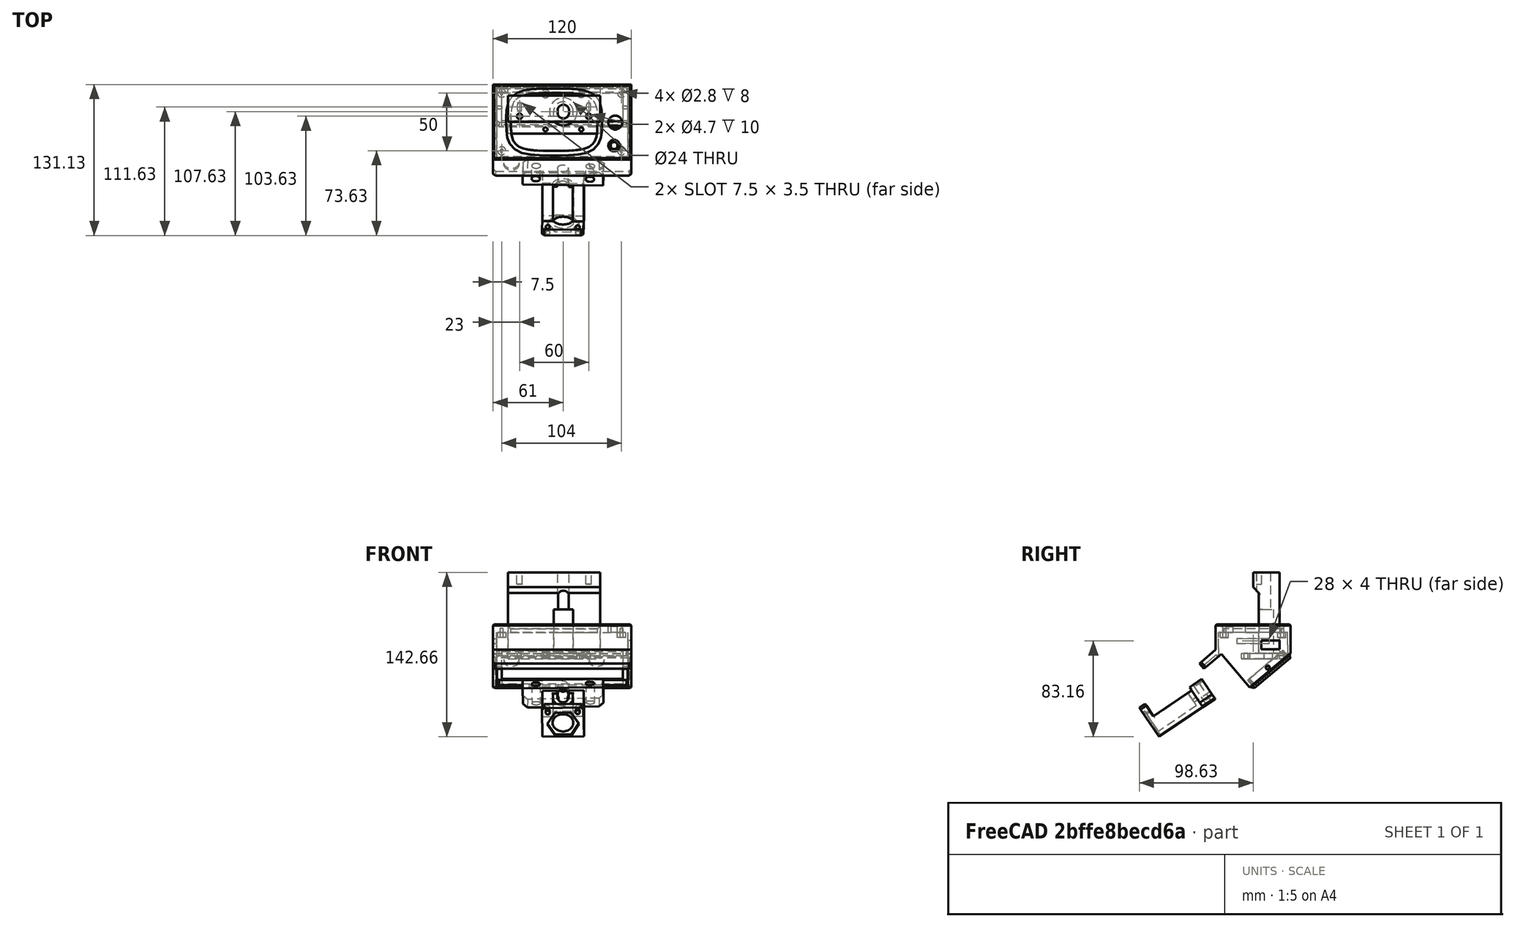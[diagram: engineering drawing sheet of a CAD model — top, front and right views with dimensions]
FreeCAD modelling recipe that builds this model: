
FCSTD DOCUMENT  (FreeCAD 0.19R)
Label: ScreenPodOnly
License: All rights reserved
LicenseURL: http://en.wikipedia.org/wiki/All_rights_reserved
objects: Sketcher::SketchObject×35, PartDesign::Pocket×24, PartDesign::Chamfer×12, PartDesign::Pad×10, PartDesign::Body×5, PartDesign::Fillet×2, Mesh::Feature×2, PartDesign::Mirrored×1
note: 137 computed .brp shape members not serialized (recipe doc carries the construction recipe); baked Part::Feature solids carry a one-line shape summary decoded from their .brp

FEATURE [Sketcher::SketchObject] Sketch
  FullyConstrained = true
  MapMode = 5
  Support = -> [XY_Plane]
  sketch-geometry (30):
    g0: LineSegment StartX=-53 StartY=32.5 StartZ=0 EndX=67 EndY=32.5 EndZ=0
    g1: LineSegment StartX=67 StartY=32.5 StartZ=0 EndX=67 EndY=-32.5 EndZ=0
    g2: LineSegment StartX=67 StartY=-32.5 StartZ=0 EndX=-53 EndY=-32.5 EndZ=0
    g3: LineSegment StartX=-53 StartY=-32.5 StartZ=0 EndX=-53 EndY=32.5 EndZ=0
    g4: LineSegment StartX=-37 StartY=24.5 StartZ=0 EndX=37 EndY=24.5 EndZ=0
    g5: LineSegment StartX=37 StartY=24.5 StartZ=0 EndX=37 EndY=-24.5 EndZ=0
    g6: LineSegment StartX=37 StartY=-24.5 StartZ=0 EndX=-37 EndY=-24.5 EndZ=0
    g7: LineSegment StartX=-37 StartY=-24.5 StartZ=0 EndX=-37 EndY=24.5 EndZ=0
    g8: LineSegment StartX=-37.7408 StartY=25.116 StartZ=0 EndX=37.7408 EndY=25.116 EndZ=0
    g9: LineSegment StartX=37.7408 StartY=25.116 StartZ=0 EndX=37.7408 EndY=-25.116 EndZ=0
    g10: LineSegment StartX=37.7408 StartY=-25.116 StartZ=0 EndX=-37.7408 EndY=-25.116 EndZ=0
    g11: LineSegment StartX=-37.7408 StartY=-25.116 StartZ=0 EndX=-37.7408 EndY=25.116 EndZ=0
    g12-g19: Circle x8 (B-spline internal-alignment scaffolding for g20; pole/knot coordinates omitted)
    g20: BSplineCurve PolesCount=8 KnotsCount=9 Degree=3 IsPeriodic=1
    g21-g29: GeomPoint x9 (B-spline internal-alignment scaffolding for g20; pole/knot coordinates omitted)
  constraints (53):
    c: Coincident(g0,g1)
    c: Coincident(g1,g2)
    c: Coincident(g2,g3)
    c: Coincident(g3,g0)
    c: Horizontal(g0)
    c: Horizontal(g2)
    c: Vertical(g1)
    c: Vertical(g3)
    c: Coincident(g4,g5)
    c: Coincident(g5,g6)
    c: Coincident(g6,g7)
    c: Coincident(g7,g4)
    c: Horizontal(g4)
    c: Vertical(g7)
    c: Distance(g5) = 49
    c: Distance(g4,g3) = 16
    c: Distance(g0,g5) = 30
    c: Distance(g6,g2) = 8
    c: Distance(g4,g0) = 8
    c: Distance(g6) = 74
    c: Symmetric(g5,g6,g-2)
    c: Symmetric(g5,g4,g-1)
    c: Coincident(g8,g9)
    c: Coincident(g9,g10)
    c: Coincident(g10,g11)
    c: Coincident(g11,g8)
    c: Horizontal(g8)
    c: Horizontal(g10)
    c: Vertical(g9)
    c: Vertical(g11)
    c: Symmetric(g9,g8,g-1)
    c: Weight(g12) = 1
    c: Equal(g12,g13)
    c: Equal(g12,g14)
    c: Equal(g12,g15)
    c: PointOnObject(g15,g-1)
    c: Equal(g12,g16)
    c: Equal(g12,g17)
    c: PointOnObject(g17,g-2)
    c: Equal(g12,g18)
    c: Equal(g12,g19)
    c: InternalAlignment(g12-g19 -> g20) x8
    c: InternalAlignment(g21-g29 -> g20) x9
    c: Coincident(g8,g12)
    c: Coincident(g14,g8)
    c: Coincident(g16,g10)
    c: Coincident(g18,g9)
    c: Distance(g19,g5) = 0.5
    c: Symmetric(g19,g15,g-2)
    c: Distance(g17,g6) = 0.5
    c: Symmetric(g17,g13,g-1)
    c: DistanceX(g8) = 37.7408
    c: DistanceY(g8) = 25.116
FEATURE [PartDesign::Pad] Pad
  Direction = (1,1,1)
  Length = 25
  Length2 = 100
  Profile = -> Sketch
  Type = 0
FEATURE [Sketcher::SketchObject] Sketch004  label="knob"
  FullyConstrained = false
  MapMode = 5
  Placement = pos=(0,0,0) rot=(1,0,0;3.14159rad)
  sketch-geometry (1):
    g0: Circle CenterX=52 CenterY=20.5 CenterZ=0 NormalX=0 NormalY=0 NormalZ=1 AngleXU=0 Radius=3
  constraints (1):
    c: Diameter(g0) = 6
FEATURE [PartDesign::Pocket] Pocket001
  BaseFeature = -> Pad
  Length = 5
  Length2 = 100
  Profile = -> Sketch004
  Type = 1
FEATURE [Sketcher::SketchObject] Sketch001  label="knob001"
  FullyConstrained = false
  MapMode = 5
  Placement = pos=(0,0,25) rot=(0,0,1;0rad)
  Support = -> [Pocket001]
  sketch-geometry (1):
    g0: Circle CenterX=53 CenterY=-0.5 CenterZ=0 NormalX=0 NormalY=0 NormalZ=1 AngleXU=0 Radius=6
  constraints (2):
    c: Diameter(g0) = 12
    c: DistanceY(g0) = -0.5
FEATURE [PartDesign::Pocket] Pocket
  BaseFeature = -> Pocket001
  Length = 5
  Length2 = 100
  Profile = -> Sketch001
  Type = 1
FEATURE [Sketcher::SketchObject] Sketch005
  FullyConstrained = true
  MapMode = 5
  Placement = pos=(0,0,0) rot=(1,0,0;3.14159rad)
  Support = -> [Pocket]
  sketch-geometry (4):
    g0: LineSegment StartX=-50 StartY=30 StartZ=0 EndX=64 EndY=30 EndZ=0
    g1: LineSegment StartX=64 StartY=30 StartZ=0 EndX=64 EndY=-30 EndZ=0
    g2: LineSegment StartX=64 StartY=-30 StartZ=0 EndX=-50 EndY=-30 EndZ=0
    g3: LineSegment StartX=-50 StartY=-30 StartZ=0 EndX=-50 EndY=30 EndZ=0
  constraints (11):
    c: Coincident(g0,g1)
    c: Coincident(g1,g2)
    c: Coincident(g2,g3)
    c: Coincident(g3,g0)
    c: Horizontal(g0)
    c: Horizontal(g2)
    c: Vertical(g1)
    c: Symmetric(g2,g0,g-1)
    c: DistanceX(g0) = -50
    c: DistanceY(g0) = 30
    c: DistanceX(g1) = 64
FEATURE [PartDesign::Pocket] Pocket002
  BaseFeature = -> Pocket
  Length = 18
  Length2 = 100
  Profile = -> Sketch005
  Type = 0
FEATURE [PartDesign::Chamfer] Chamfer
  Angle = 45
  Base = -> Pocket002 [Edge19]
  BaseFeature = -> Pocket002
  ChamferType = 0
  FlipDirection = false
  Size = 4
  Size2 = 1
  SupportTransform = false
FEATURE [Sketcher::SketchObject] Sketch006  label="standofs"
  FullyConstrained = true
  MapMode = 5
  Placement = pos=(0,0,18) rot=(1,0,0;3.14159rad)
  Support = -> [Chamfer]
  sketch-geometry (4):
    g0: Circle CenterX=-45.5 CenterY=25 CenterZ=0 NormalX=0 NormalY=0 NormalZ=1 AngleXU=0 Radius=3.5
    g1: Circle CenterX=-45.5 CenterY=-25 CenterZ=0 NormalX=0 NormalY=0 NormalZ=1 AngleXU=0 Radius=3.5
    g2: Circle CenterX=58.5 CenterY=-25 CenterZ=0 NormalX=0 NormalY=0 NormalZ=1 AngleXU=0 Radius=3.5
    g3: Circle CenterX=58.5 CenterY=25 CenterZ=0 NormalX=0 NormalY=0 NormalZ=1 AngleXU=0 Radius=3.5
  constraints (10):
    c: Diameter(g0) = 7
    c: Equal(g0,g1)
    c: Equal(g0,g3)
    c: Equal(g0,g2)
    c: Symmetric(g1,g0,g-1)
    c: Symmetric(g2,g3,g-1)
    c: Distance(g3,g2) = 50
    c: Distance(g1,g0) = 50
    c: Distance(g3,g0) = 104
    c: DistanceX(g0) = -45.5
FEATURE [PartDesign::Pad] Pad001
  BaseFeature = -> Chamfer
  Direction = (1,1,1)
  Length = 4.5
  Length2 = 100
  Profile = -> Sketch006
  Type = 0
FEATURE [Sketcher::SketchObject] Sketch007  label="holes"
  FullyConstrained = true
  MapMode = 5
  Placement = pos=(0,0,13.5) rot=(1,0,0;3.14159rad)
  Support = -> [Pad001]
  sketch-geometry (4):
    g0: Circle CenterX=-45.5 CenterY=25 CenterZ=0 NormalX=0 NormalY=0 NormalZ=1 AngleXU=0 Radius=1.4
    g1: Circle CenterX=58.5 CenterY=25 CenterZ=0 NormalX=0 NormalY=0 NormalZ=1 AngleXU=0 Radius=1.4
    g2: Circle CenterX=58.5 CenterY=-25 CenterZ=0 NormalX=0 NormalY=0 NormalZ=1 AngleXU=0 Radius=1.4
    g3: Circle CenterX=-45.5 CenterY=-25 CenterZ=0 NormalX=0 NormalY=0 NormalZ=1 AngleXU=0 Radius=1.4
  constraints (10):
    c: Distance(g3,g2) = 104
    c: Distance(g3,g0) = 50
    c: Symmetric(g3,g0,g-1)
    c: Symmetric(g2,g1,g-1)
    c: Diameter(g1) = 2.8
    c: Equal(g1,g2)
    c: Equal(g1,g3)
    c: Equal(g1,g0)
    c: DistanceX(g0) = -45.5
    c: Distance(g1,g2) = 50
FEATURE [PartDesign::Pocket] Pocket003
  BaseFeature = -> Pad001
  Length = 8
  Length2 = 100
  Profile = -> Sketch007
  Type = 0
FEATURE [Sketcher::SketchObject] Sketch008
  ExternalGeometry = -> [Pocket003]
  FullyConstrained = true
  MapMode = 5
  Placement = pos=(67,0,0) rot=(0.57735,0.57735,0.57735;2.0944rad)
  Support = -> [Pocket003]
  sketch-geometry (4):
    g0: LineSegment StartX=7 StartY=6.5 StartZ=0 EndX=23 EndY=6.5 EndZ=0
    g1: LineSegment StartX=23 StartY=6.5 StartZ=0 EndX=23 EndY=0 EndZ=0
    g2: LineSegment StartX=23 StartY=0 StartZ=0 EndX=7 EndY=0 EndZ=0
    g3: LineSegment StartX=7 StartY=0 StartZ=0 EndX=7 EndY=6.5 EndZ=0
  constraints (12):
    c: Coincident(g0,g1)
    c: Coincident(g1,g2)
    c: Coincident(g2,g3)
    c: Coincident(g3,g0)
    c: Horizontal(g0)
    c: Horizontal(g2)
    c: Vertical(g1)
    c: Vertical(g3)
    c: Distance(g-3,g0) = 7
    c: Distance(g0) = 16
    c: Distance(g0,g-4) = 7
    c: PointOnObject(g1,g-1)
FEATURE [PartDesign::Pocket] Pocket004
  BaseFeature = -> Pocket003
  Length = 9
  Length2 = 100
  Profile = -> Sketch008
  Type = 0
FEATURE [Sketcher::SketchObject] Sketch009
  ExternalGeometry = -> [Pocket004]
  FullyConstrained = true
  MapMode = 5
  Placement = pos=(-53,0,0) rot=(0.57735,-0.57735,-0.57735;2.0944rad)
  Support = -> [Pocket004]
  sketch-geometry (4):
    g0: LineSegment StartX=-14 StartY=12.5 StartZ=0 EndX=14 EndY=12.5 EndZ=0
    g1: LineSegment StartX=14 StartY=12.5 StartZ=0 EndX=14 EndY=8.5 EndZ=0
    g2: LineSegment StartX=14 StartY=8.5 StartZ=0 EndX=-14 EndY=8.5 EndZ=0
    g3: LineSegment StartX=-14 StartY=8.5 StartZ=0 EndX=-14 EndY=12.5 EndZ=0
  constraints (11):
    c: Coincident(g0,g1)
    c: Coincident(g1,g2)
    c: Coincident(g2,g3)
    c: Coincident(g3,g0)
    c: Horizontal(g0)
    c: Vertical(g1)
    c: Vertical(g3)
    c: Distance(g0,g-3) = 1
    c: Distance(g1) = 4
    c: Symmetric(g1,g2,g-2)
    c: Distance(g2) = 28
FEATURE [PartDesign::Pocket] Pocket005
  BaseFeature = -> Pocket004
  Length = 5
  Length2 = 100
  Profile = -> Sketch009
  Type = 0
FEATURE [Sketcher::SketchObject] Sketch010
  FullyConstrained = false
  MapMode = 5
  Placement = pos=(-53,0,0) rot=(0.57735,-0.57735,-0.57735;2.0944rad)
  Support = -> [Pocket005]
  sketch-geometry (8):
    g0: LineSegment StartX=2.97644 StartY=-29.7683 StartZ=0 EndX=27.4024 EndY=-0.658582 EndZ=0
    g1: LineSegment StartX=27.4024 StartY=-0.658582 StartZ=0 EndX=42.7233 EndY=-13.5143 EndZ=0
    g2: LineSegment StartX=42.7233 StartY=-13.5143 StartZ=0 EndX=46.58 EndY=-8.91807 EndZ=0
    g3: LineSegment StartX=46.58 StartY=-8.91807 StartZ=0 EndX=27.4809 EndY=7.10801 EndZ=0
    g4: LineSegment StartX=-32.5 StartY=0 StartZ=0 EndX=2.97644 EndY=-29.7683 EndZ=0
    g5: LineSegment StartX=2.97644 StartY=-29.7683 StartZ=0 EndX=-60.5281 EndY=23.5183 EndZ=0
    g6: LineSegment StartX=27.4809 StartY=7.10801 StartZ=0 EndX=-32.5 EndY=7.10801 EndZ=0
    g7: LineSegment StartX=-32.5 StartY=7.10801 StartZ=0 EndX=-32.5 EndY=0 EndZ=0
  constraints (21):
    c: Coincident(g0,g1)
    c: Perpendicular(g1,g0)
    c: Coincident(g1,g2)
    c: Coincident(g2,g3)
    c: Coincident(g4,g0)
    c: Distance(g0) = 38
    c: Parallel(g1,g3)
    c: Perpendicular(g0,g4)
    c: Perpendicular(g1,g2)
    c: Distance(g2) = 6
    c: Angle(g0) = 0.872665
    c: Coincident(g5,g0)
    c: Perpendicular(g0,g5)
    c: PointOnObject(g4,g-1)
    c: Distance(g1) = 20
    c: Coincident(g6,g3)
    c: Horizontal(g6)
    c: DistanceX(g6) = -32.5
    c: Coincident(g7,g6)
    c: Vertical(g7)
    c: Coincident(g4,g7)
FEATURE [PartDesign::Pad] Pad002
  BaseFeature = -> Pocket005
  Direction = (1,1,1)
  Length = 120
  Length2 = 100
  Profile = -> Sketch010
  Reversed = true
  Type = 0
FEATURE [Sketcher::SketchObject] Sketch015
  FullyConstrained = true
  MapMode = 5
  Placement = pos=(0,0,13.5) rot=(1,0,0;3.14159rad)
  sketch-geometry (4):
    g0: LineSegment StartX=-50 StartY=30 StartZ=0 EndX=64 EndY=30 EndZ=0
    g1: LineSegment StartX=64 StartY=30 StartZ=0 EndX=64 EndY=-30 EndZ=0
    g2: LineSegment StartX=64 StartY=-30 StartZ=0 EndX=-50 EndY=-30 EndZ=0
    g3: LineSegment StartX=-50 StartY=-30 StartZ=0 EndX=-50 EndY=30 EndZ=0
  constraints (11):
    c: Coincident(g0,g1)
    c: Coincident(g1,g2)
    c: Coincident(g2,g3)
    c: Coincident(g3,g0)
    c: Horizontal(g0)
    c: Horizontal(g2)
    c: Vertical(g1)
    c: DistanceX(g0) = 64
    c: DistanceX(g0) = -50
    c: Distance(g3) = 60
    c: Symmetric(g2,g0,g-1)
FEATURE [PartDesign::Pocket] Pocket006
  BaseFeature = -> Pad002
  Length = 47
  Length2 = 100
  Profile = -> Sketch015
  Reversed = true
  Type = 0
FEATURE [Sketcher::SketchObject] Sketch016
  FullyConstrained = true
  MapMode = 5
  Placement = pos=(67,0,0) rot=(0.57735,0.57735,0.57735;2.0944rad)
  Support = -> [Pocket006]
  sketch-geometry (4):
    g0: LineSegment StartX=7 StartY=11 StartZ=0 EndX=23 EndY=11 EndZ=0
    g1: LineSegment StartX=23 StartY=11 StartZ=0 EndX=23 EndY=3.5 EndZ=0
    g2: LineSegment StartX=23 StartY=3.5 StartZ=0 EndX=7 EndY=3.5 EndZ=0
    g3: LineSegment StartX=7 StartY=3.5 StartZ=0 EndX=7 EndY=11 EndZ=0
  constraints (12):
    c: Coincident(g0,g1)
    c: Coincident(g1,g2)
    c: Coincident(g2,g3)
    c: Coincident(g3,g0)
    c: Horizontal(g0)
    c: Horizontal(g2)
    c: Vertical(g1)
    c: Vertical(g3)
    c: Distance(g1) = 7.5
    c: Distance(g2) = 16
    c: DistanceX(g0) = 7
    c: DistanceY(g0) = 11
FEATURE [PartDesign::Pocket] Pocket007
  BaseFeature = -> Pocket006
  Length = 9
  Length2 = 100
  Profile = -> Sketch016
  Type = 0
FEATURE [PartDesign::Chamfer] Chamfer001
  Angle = 45
  Base = -> Pocket007 [Edge6]
  BaseFeature = -> Pocket007
  ChamferType = 0
  FlipDirection = false
  Size = 2
  Size2 = 1
  SupportTransform = false
FEATURE [Sketcher::SketchObject] Sketch017
  ExternalGeometry = -> [Chamfer001]
  FullyConstrained = false
  MapMode = 5
  Placement = pos=(0,13.4282,-16.0031) rot=(1,0,0;3.83972rad)
  Support = -> [Chamfer001]
  sketch-geometry (4):
    g0: LineSegment StartX=-53 StartY=-24.6078 StartZ=0 EndX=67 EndY=-24.6078 EndZ=0
    g1: LineSegment StartX=67 StartY=-24.6078 StartZ=0 EndX=67 EndY=20.3922 EndZ=0
    g2: LineSegment StartX=67 StartY=20.3922 StartZ=0 EndX=-53 EndY=20.3922 EndZ=0
    g3: LineSegment StartX=-53 StartY=20.3922 StartZ=0 EndX=-53 EndY=-24.6078 EndZ=0
  constraints (11):
    c: Coincident(g0,g1)
    c: Coincident(g1,g2)
    c: Coincident(g2,g3)
    c: Coincident(g3,g0)
    c: Horizontal(g0)
    c: Horizontal(g2)
    c: Vertical(g1)
    c: Vertical(g3)
    c: Distance(g2) = 120
    c: DistanceX(g2) = -53
    c: Distance(g3) = 45
FEATURE [Sketcher::SketchObject] Sketch018
  FullyConstrained = true
  MapMode = 5
  Placement = pos=(0,0,0) rot=(1,0,0;1.5708rad)
  Support = -> [XZ_Plane001]
  sketch-geometry (4):
    g0: LineSegment StartX=-60 StartY=22.5 StartZ=0 EndX=60 EndY=22.5 EndZ=0
    g1: LineSegment StartX=60 StartY=22.5 StartZ=0 EndX=60 EndY=-22.5 EndZ=0
    g2: LineSegment StartX=60 StartY=-22.5 StartZ=0 EndX=-60 EndY=-22.5 EndZ=0
    g3: LineSegment StartX=-60 StartY=-22.5 StartZ=0 EndX=-60 EndY=22.5 EndZ=0
  constraints (10):
    c: Coincident(g0,g1)
    c: Coincident(g1,g2)
    c: Coincident(g2,g3)
    c: Coincident(g3,g0)
    c: Horizontal(g2)
    c: Vertical(g3)
    c: Symmetric(g0,g0,g-2)
    c: Distance(g0) = 120
    c: Distance(g1) = 45
    c: Symmetric(g1,g0,g-1)
FEATURE [PartDesign::Pad] Pad003
  Direction = (1,1,1)
  Length = 3
  Length2 = 100
  Placement = pos=(0,0,0) rot=(1,0,0;1.5708rad)
  Profile = -> Sketch018
  Type = 0
FEATURE [Sketcher::SketchObject] Sketch019
  FullyConstrained = true
  MapMode = 5
  Placement = pos=(0,-3,7e-16) rot=(1,0,0;1.5708rad)
  Support = -> [Pad003]
  sketch-geometry (4):
    g0: LineSegment StartX=-56.75 StartY=20 StartZ=0 EndX=56.75 EndY=20 EndZ=0
    g1: LineSegment StartX=56.75 StartY=20 StartZ=0 EndX=56.75 EndY=-20 EndZ=0
    g2: LineSegment StartX=56.75 StartY=-20 StartZ=0 EndX=-56.75 EndY=-20 EndZ=0
    g3: LineSegment StartX=-56.75 StartY=-20 StartZ=0 EndX=-56.75 EndY=20 EndZ=0
  constraints (11):
    c: Coincident(g0,g1)
    c: Coincident(g1,g2)
    c: Coincident(g2,g3)
    c: Coincident(g3,g0)
    c: Horizontal(g0)
    c: Horizontal(g2)
    c: Vertical(g1)
    c: Vertical(g3)
    c: Distance(g0) = 113.5
    c: Distance(g1) = 40
    c: Symmetric(g1,g0,g-1)
FEATURE [PartDesign::Pad] Pad004
  BaseFeature = -> Pad003
  Direction = (1,1,1)
  Length = 6
  Length2 = 100
  Placement = pos=(0,0,0) rot=(1,0,0;1.5708rad)
  Profile = -> Sketch019
  Type = 0
FEATURE [Sketcher::SketchObject] Sketch020
  FullyConstrained = true
  MapMode = 5
  Placement = pos=(56.75,0,0) rot=(0.707107,0,0.707107;3.14159rad)
  Support = -> [Pad004]
  sketch-geometry (1):
    g0: Circle CenterX=0 CenterY=6 CenterZ=0 NormalX=0 NormalY=0 NormalZ=1 AngleXU=0 Radius=1.4
  constraints (3):
    c: PointOnObject(g0,g-2)
    c: Diameter(g0) = 2.8
    c: DistanceY(g0) = 6
FEATURE [PartDesign::Pocket] Pocket008
  BaseFeature = -> Pad004
  Length = 5
  Length2 = 100
  Placement = pos=(0,0,0) rot=(1,0,0;1.5708rad)
  Profile = -> Sketch020
  Type = 1
FEATURE [Sketcher::SketchObject] Sketch021
  FullyConstrained = true
  MapMode = 5
  Placement = pos=(0,-9,1.5e-14) rot=(1,0,0;1.5708rad)
  sketch-geometry (4):
    g0: LineSegment StartX=-52.5 StartY=18.5 StartZ=0 EndX=52.5 EndY=18.5 EndZ=0
    g1: LineSegment StartX=52.5 StartY=18.5 StartZ=0 EndX=52.5 EndY=-18.5 EndZ=0
    g2: LineSegment StartX=52.5 StartY=-18.5 StartZ=0 EndX=-52.5 EndY=-18.5 EndZ=0
    g3: LineSegment StartX=-52.5 StartY=-18.5 StartZ=0 EndX=-52.5 EndY=18.5 EndZ=0
  constraints (11):
    c: Coincident(g0,g1)
    c: Coincident(g1,g2)
    c: Coincident(g2,g3)
    c: Coincident(g3,g0)
    c: Horizontal(g0)
    c: Horizontal(g2)
    c: Vertical(g1)
    c: Vertical(g3)
    c: Distance(g0) = 105
    c: Symmetric(g0,g2,g-1)
    c: Distance(g1) = 37
FEATURE [Sketcher::SketchObject] Sketch022
  ExternalGeometry = -> [Chamfer001]
  FullyConstrained = true
  MapMode = 5
  Placement = pos=(-53,0,0) rot=(0.57735,-0.57735,-0.57735;2.0944rad)
  Support = -> [Chamfer001]
  sketch-geometry (2):
    g0: Circle CenterX=-12.8334 CenterY=-12.586 CenterZ=0 NormalX=0 NormalY=0 NormalZ=1 AngleXU=0 Radius=1.75
    g1: LineSegment StartX=-30.5716 StartY=2.29813 StartZ=0 EndX=4.90481 EndY=-27.4701 EndZ=0
  constraints (6):
    c: Parallel(g1,g-3)
    c: Distance(g1,g-3) = 3
    c: Equal(g1,g-3)
    c: Symmetric(g1,g1,g0)
    c: Diameter(g0) = 3.5
    c: PointOnObject(g1,g-4)
FEATURE [PartDesign::Pocket] Pocket010
  BaseFeature = -> Chamfer001
  Length = 5
  Length2 = 100
  Profile = -> Sketch022
  Type = 1
FEATURE [PartDesign::Chamfer] Chamfer005
  Angle = 45
  Base = -> Pocket010 [Edge97]
  BaseFeature = -> Pocket010
  ChamferType = 0
  FlipDirection = false
  Size = 2
  Size2 = 1
  SupportTransform = false
FEATURE [PartDesign::Chamfer] Chamfer006
  Angle = 45
  Base = -> Chamfer005 [Edge23]
  BaseFeature = -> Chamfer005
  ChamferType = 0
  FlipDirection = false
  Size = 2
  Size2 = 1
  SupportTransform = false
FEATURE [Sketcher::SketchObject] Sketch023
  FullyConstrained = true
  MapMode = 5
  Placement = pos=(0,-10.9977,13.1066) rot=(1,0,0;3.83972rad)
  Support = -> [Chamfer006]
  sketch-geometry (2):
    g0: Circle CenterX=-37 CenterY=32 CenterZ=0 NormalX=0 NormalY=0 NormalZ=1 AngleXU=0 Radius=6.5
    g1: Circle CenterX=37 CenterY=32 CenterZ=0 NormalX=0 NormalY=0 NormalZ=1 AngleXU=0 Radius=6.5
  constraints (5):
    c: Diameter(g1) = 13
    c: Equal(g1,g0)
    c: Symmetric(g1,g0,g-2)
    c: DistanceY(g0) = 32
    c: Distance(g1,g0) = 74
FEATURE [PartDesign::Pocket] Pocket011
  BaseFeature = -> Chamfer006
  Length = 2.3
  Length2 = 100
  Profile = -> Sketch023
  Type = 0
FEATURE [PartDesign::Chamfer] Chamfer007
  Angle = 45
  Base = -> Pocket011 [Edge74,Edge75,Edge31,Edge67]
  BaseFeature = -> Pocket011
  ChamferType = 0
  FlipDirection = false
  Size = 1
  Size2 = 1
  SupportTransform = false
FEATURE [PartDesign::Body] Body  label="ScreenBox"
  Group = -> [Sketch,Pad,Sketch001,Sketch004,Pocket001,Pocket,Sketch005,Pocket002,Chamfer,Sketch006,Pad001,Sketch007,Pocket003,Sketch008,Pocket004,Sketch009,Pocket005,Sketch010,Pad002,Sketch015,Pocket006,Sketch016,Pocket007,Chamfer001,Sketch017,Sketch022,Pocket010,Chamfer005,Chamfer006,Sketch023,Pocket011,Chamfer007]
  Origin = -> Origin
  Tip = -> Chamfer007
FEATURE [Sketcher::SketchObject] Sketch024
  ExternalGeometry = -> [Pocket008]
  FullyConstrained = false
  MapMode = 5
  Placement = pos=(60,0,0) rot=(0.707107,0,0.707107;3.14159rad)
  Support = -> [Pocket008]
  sketch-geometry (3):
    g0: LineSegment StartX=-22.5 StartY=3 StartZ=0 EndX=-17.8755 EndY=-3.60453 EndZ=0
    g1: LineSegment StartX=-17.8755 StartY=-3.60453 StartZ=0 EndX=-35.5163 EndY=-3.60453 EndZ=0
    g2: LineSegment StartX=-35.5163 StartY=-3.60453 StartZ=0 EndX=-22.5 EndY=3 EndZ=0
  constraints (6):
    c: Coincident(g0,g1)
    c: Horizontal(g1)
    c: Coincident(g1,g2)
    c: Coincident(g2,g0)
    c: Angle(g0) = -0.959931
    c: Coincident(g0,g-3)
FEATURE [PartDesign::Pocket] Pocket012
  BaseFeature = -> Pocket008
  Length = 5
  Length2 = 100
  Placement = pos=(0,0,0) rot=(1,0,0;1.5708rad)
  Profile = -> Sketch024
  Type = 1
FEATURE [PartDesign::Mirrored] Mirrored
  BaseFeature = -> Pocket012
  MirrorPlane = -> Sketch024 [V_Axis]
  Originals = -> [Pocket012]
  Placement = pos=(0,0,0) rot=(1,0,0;1.5708rad)
FEATURE [PartDesign::Chamfer] Chamfer008
  Angle = 45
  Base = -> Mirrored [Edge14,Edge12]
  BaseFeature = -> Mirrored
  ChamferType = 0
  FlipDirection = false
  Placement = pos=(0,0,0) rot=(1,0,0;1.5708rad)
  Size = 2
  Size2 = 1
  SupportTransform = false
FEATURE [PartDesign::Pocket] Pocket013
  BaseFeature = -> Chamfer008
  Length = 6
  Length2 = 100
  Placement = pos=(0,0,0) rot=(1,0,0;1.5708rad)
  Profile = -> Sketch021
  Type = 0
FEATURE [PartDesign::Chamfer] Chamfer009
  Angle = 45
  Base = -> Pocket013 [Edge29]
  BaseFeature = -> Pocket013
  ChamferType = 0
  FlipDirection = false
  Placement = pos=(0,0,0) rot=(1,0,0;1.5708rad)
  Size = 2
  Size2 = 1
  SupportTransform = false
FEATURE [PartDesign::Chamfer] Chamfer010
  Angle = 45
  Base = -> Chamfer009 [Edge11]
  BaseFeature = -> Chamfer009
  ChamferType = 0
  FlipDirection = false
  Placement = pos=(0,0,0) rot=(1,0,0;1.5708rad)
  Size = 1
  Size2 = 1
  SupportTransform = false
FEATURE [PartDesign::Chamfer] Chamfer011
  Angle = 45
  Base = -> Chamfer010 [Edge18]
  BaseFeature = -> Chamfer010
  ChamferType = 0
  FlipDirection = false
  Placement = pos=(0,0,0) rot=(1,0,0;1.5708rad)
  Size = 1
  Size2 = 1
  SupportTransform = false
FEATURE [PartDesign::Chamfer] Chamfer012
  Angle = 45
  Base = -> Chamfer011 [Edge20]
  BaseFeature = -> Chamfer011
  ChamferType = 0
  FlipDirection = false
  Placement = pos=(0,0,0) rot=(1,0,0;1.5708rad)
  Size = 2
  Size2 = 1
  SupportTransform = false
FEATURE [PartDesign::Body] Body001  label="BoxCap"
  Group = -> [Sketch018,Pad003,Sketch019,Pad004,Sketch020,Pocket008,Sketch021,Sketch024,Pocket012,Mirrored,Chamfer008,Pocket013,Chamfer009,Chamfer010,Chamfer011,Chamfer012]
  Origin = -> Origin001
  Placement = pos=(7,16.6296,-17.3502) rot=(-1,0,0;0.872665rad)
  Tip = -> Chamfer012
FEATURE [Sketcher::SketchObject] Sketch025  label="mountSlots"
  FullyConstrained = true
  MapMode = 5
  Placement = pos=(0,20.9938,0) rot=(0,0.707107,0.707107;3.14159rad)
  sketch-geometry (9):
    g0: ArcOfCircle CenterX=-16.5 CenterY=6.35 CenterZ=0 NormalX=0 NormalY=0 NormalZ=1 AngleXU=0 Radius=2.6 StartAngle=1.5708 EndAngle=4.71239
    g1: ArcOfCircle CenterX=-14.5 CenterY=6.35 CenterZ=0 NormalX=0 NormalY=0 NormalZ=1 AngleXU=0 Radius=2.6 StartAngle=4.71239 EndAngle=7.85398
    g2: LineSegment StartX=-16.5 StartY=3.75 StartZ=0 EndX=-14.5 EndY=3.75 EndZ=0
    g3: LineSegment StartX=-16.5 StartY=8.95 StartZ=0 EndX=-14.5 EndY=8.95 EndZ=0
    g4: ArcOfCircle CenterX=30.5 CenterY=6.35 CenterZ=0 NormalX=0 NormalY=0 NormalZ=1 AngleXU=0 Radius=2.6 StartAngle=1.5708 EndAngle=4.71239
    g5: ArcOfCircle CenterX=32.5 CenterY=6.35 CenterZ=0 NormalX=0 NormalY=0 NormalZ=1 AngleXU=0 Radius=2.6 StartAngle=4.71239 EndAngle=7.85398
    g6: LineSegment StartX=30.5 StartY=3.75 StartZ=0 EndX=32.5 EndY=3.75 EndZ=0
    g7: LineSegment StartX=30.5 StartY=8.95 StartZ=0 EndX=32.5 EndY=8.95 EndZ=0
    g8: Circle CenterX=8 CenterY=6.35 CenterZ=0 NormalX=0 NormalY=0 NormalZ=1 AngleXU=0 Radius=0.77
  constraints (22):
    c: Tangent(g0,g3) = 1.5708
    c: Tangent(g0,g2) = -1.5708
    c: Tangent(g2,g1) = -1.5708
    c: Tangent(g3,g1) = 1.5708
    c: Horizontal(g2)
    c: Equal(g0,g1)
    c: Tangent(g4,g7) = 1.5708
    c: Tangent(g4,g6) = -1.5708
    c: Tangent(g6,g5) = -1.5708
    c: Tangent(g7,g5) = 1.5708
    c: Horizontal(g6)
    c: Equal(g4,g5)
    c: Distance(g1,g1) = 5.2
    c: Distance(g5,g5) = 5.2
    c: DistanceY(g1) = 6.35
    c: Distance(g6) = 2
    c: Distance(g2) = 2
    c: Distance(g1,g4) = 45
    c: Symmetric(g1,g4,g8)
    c: DistanceX(g8) = 8
    c: DistanceY(g5) = 6.35
    c: Diameter(g8) = 1.54
FEATURE [Sketcher::SketchObject] Sketch026  label="hex"
  FullyConstrained = true
  MapMode = 5
  Placement = pos=(0,0,56.7) rot=(0,0,1;0rad)
  sketch-geometry (8):
    g0: Circle CenterX=-8 CenterY=5 CenterZ=0 NormalX=0 NormalY=0 NormalZ=1 AngleXU=0 Radius=11
    g1: LineSegment StartX=5.85641 StartY=5 StartZ=0 EndX=-1.0718 EndY=17 EndZ=0
    g2: LineSegment StartX=-1.0718 StartY=17 StartZ=0 EndX=-14.9282 EndY=17 EndZ=0
    g3: LineSegment StartX=-14.9282 StartY=17 StartZ=0 EndX=-21.8564 EndY=5 EndZ=0
    g4: LineSegment StartX=-21.8564 StartY=5 StartZ=0 EndX=-14.9282 EndY=-7 EndZ=0
    g5: LineSegment StartX=-14.9282 StartY=-7 StartZ=0 EndX=-1.0718 EndY=-7 EndZ=0
    g6: LineSegment StartX=-1.0718 StartY=-7 StartZ=0 EndX=5.85641 EndY=5 EndZ=0
    g7: Circle CenterX=-8 CenterY=5 CenterZ=0 NormalX=0 NormalY=0 NormalZ=1 AngleXU=0 Radius=13.8564
  constraints (19):
    c: Diameter(g0) = 22
    c: DistanceX(g0) = -8
    c: DistanceY(g0) = 5
    c: Coincident(g1,g2)
    c: Coincident(g2,g3)
    c: Coincident(g3,g4)
    c: Coincident(g4,g5)
    c: Coincident(g5,g6)
    c: Coincident(g6,g1)
    c: Equal(g1, g2-g6) x5
    c: PointOnObject(g1,g7)
    c: PointOnObject(g2,g7)
    c: PointOnObject(g3,g7)
    c: PointOnObject(g4,g7)
    c: PointOnObject(g5,g7)
    c: PointOnObject(g6,g7)
    c: Coincident(g7,g0)
    c: Distance(g1,g4) = 24
    c: Horizontal(g2)
FEATURE [Sketcher::SketchObject] Sketch027  label="StepperPlatform"
  FullyConstrained = false
  MapMode = 5
  Placement = pos=(0,0,52.7) rot=(0,0,1;0rad)
  sketch-geometry (22):
    g0: Circle CenterX=-21 CenterY=18 CenterZ=0 NormalX=0 NormalY=0 NormalZ=1 AngleXU=0 Radius=1.4
    g1: Circle CenterX=5 CenterY=18 CenterZ=0 NormalX=0 NormalY=0 NormalZ=1 AngleXU=0 Radius=1.4
    g2: Circle CenterX=-21 CenterY=-8 CenterZ=0 NormalX=0 NormalY=0 NormalZ=1 AngleXU=0 Radius=1.4
    g3: Circle CenterX=5 CenterY=-8 CenterZ=0 NormalX=0 NormalY=0 NormalZ=1 AngleXU=0 Radius=1.4
    g4: LineSegment StartX=-21 StartY=18 StartZ=0 EndX=5 EndY=18 EndZ=0
    g5: LineSegment StartX=5 StartY=18 StartZ=0 EndX=5 EndY=-8 EndZ=0
    g6: LineSegment StartX=5 StartY=-8 StartZ=0 EndX=-21 EndY=-8 EndZ=0
    g7: LineSegment StartX=-21 StartY=-8 StartZ=0 EndX=-21 EndY=18 EndZ=0
    g8: Circle CenterX=-8 CenterY=5 CenterZ=0 NormalX=0 NormalY=0 NormalZ=1 AngleXU=0 Radius=1.66613
    g9: LineSegment StartX=-26 StartY=18 StartZ=0 EndX=10 EndY=18 EndZ=0
    g10: LineSegment StartX=10 StartY=18 StartZ=0 EndX=10 EndY=-12 EndZ=0
    g11: LineSegment StartX=10 StartY=-12 StartZ=0 EndX=-26 EndY=-12 EndZ=0
    g12: LineSegment StartX=-26 StartY=-12 StartZ=0 EndX=-26 EndY=18 EndZ=0
    g13: LineSegment StartX=-8 StartY=22.1839 StartZ=0 EndX=-8 EndY=5 EndZ=0
    g14: ArcOfCircle CenterX=-21 CenterY=-7 CenterZ=0 NormalX=0 NormalY=0 NormalZ=1 AngleXU=0 Radius=1.75 StartAngle=0 EndAngle=3.14159
    g15: ArcOfCircle CenterX=-21 CenterY=-9 CenterZ=0 NormalX=0 NormalY=0 NormalZ=1 AngleXU=0 Radius=1.75 StartAngle=3.14159 EndAngle=6.28319
    g16: LineSegment StartX=-22.75 StartY=-7 StartZ=0 EndX=-22.75 EndY=-9 EndZ=0
    g17: LineSegment StartX=-19.25 StartY=-7 StartZ=0 EndX=-19.25 EndY=-9 EndZ=0
    g18: ArcOfCircle CenterX=5 CenterY=-7 CenterZ=0 NormalX=0 NormalY=0 NormalZ=1 AngleXU=0 Radius=1.75 StartAngle=1e-16 EndAngle=3.14159
    g19: ArcOfCircle CenterX=5 CenterY=-9 CenterZ=0 NormalX=0 NormalY=0 NormalZ=1 AngleXU=0 Radius=1.75 StartAngle=3.14159 EndAngle=6.28319
    g20: LineSegment StartX=3.25 StartY=-7 StartZ=0 EndX=3.25 EndY=-9 EndZ=0
    g21: LineSegment StartX=6.75 StartY=-7 StartZ=0 EndX=6.75 EndY=-9 EndZ=0
  constraints (52):
    c: Coincident(g4,g0)
    c: Coincident(g4,g1)
    c: Horizontal(g4)
    c: Coincident(g4,g5)
    c: Coincident(g5,g3)
    c: Coincident(g5,g6)
    c: Coincident(g6,g2)
    c: Horizontal(g6)
    c: Coincident(g6,g7)
    c: Coincident(g7,g4)
    c: Distance(g7) = 26
    c: Equal(g7,g4)
    c: Equal(g4,g5)
    c: Vertical(g7)
    c: DistanceX(g8) = -8
    c: DistanceY(g8) = 5
    c: Diameter(g0) = 2.8
    c: Equal(g0,g1)
    c: Equal(g0,g3)
    c: Equal(g0,g2)
    c: Coincident(g9,g10)
    c: Coincident(g10,g11)
    c: Coincident(g11,g12)
    c: Coincident(g12,g9)
    c: Horizontal(g9)
    c: Horizontal(g11)
    c: Vertical(g10)
    c: Vertical(g12)
    c: Distance(g9) = 36
    c: Coincident(g13,g8)
    c: Tangent(g14,g17) = 1.5708
    c: Tangent(g14,g16) = -1.5708
    c: Tangent(g16,g15) = -1.5708
    c: Tangent(g17,g15) = 1.5708
    c: Vertical(g16)
    c: Equal(g14,g15)
    c: PointOnObject(g14,g7)
    c: Distance(g14,g2) = 1
    c: Distance(g15,g2) = 1
    c: Tangent(g18,g21) = 1.5708
    c: Tangent(g18,g20) = -1.5708
    c: Tangent(g20,g19) = -1.5708
    c: Tangent(g21,g19) = 1.5708
    c: Vertical(g20)
    c: Equal(g18,g19)
    c: PointOnObject(g18,g5)
    c: Distance(g18,g3) = 1
    c: Distance(g19,g3) = 1
    c: Diameter(g18) = 3.5
    c: Diameter(g14) = 3.5
    c: DistanceY(g9) = 18
    c: DistanceY(g10) = -12
FEATURE [Sketcher::SketchObject] Sketch028  label="leadSlot"
  FullyConstrained = true
  MapMode = 5
  Placement = pos=(0,0,52.7) rot=(0,0,1;0rad)
  sketch-geometry (4):
    g0: ArcOfCircle CenterX=-8 CenterY=5 CenterZ=0 NormalX=0 NormalY=0 NormalZ=1 AngleXU=0 Radius=5 StartAngle=2e-16 EndAngle=3.14159
    g1: LineSegment StartX=-3 StartY=5 StartZ=0 EndX=-3 EndY=-7.39 EndZ=0
    g2: LineSegment StartX=-3 StartY=-7.39 StartZ=0 EndX=-13 EndY=-7.39 EndZ=0
    g3: LineSegment StartX=-13 StartY=-7.39 StartZ=0 EndX=-13 EndY=5 EndZ=0
  constraints (11):
    c: Tangent(g0,g1) = 1.5708
    c: Coincident(g1,g2)
    c: Horizontal(g2)
    c: Coincident(g2,g3)
    c: Vertical(g3)
    c: Diameter(g0) = 10
    c: Vertical(g1)
    c: DistanceX(g0) = -8
    c: DistanceY(g0) = 5
    c: Tangent(g3,g0) = 1.5708
    c: Distance(g1) = 12.39
FEATURE [Sketcher::SketchObject] Sketch029  label="BottomBit"
  FullyConstrained = false
  MapMode = 5
  Support = -> [XY_Plane002]
  sketch-geometry (5):
    g0: LineSegment StartX=-43 StartY=18 StartZ=0 EndX=27 EndY=18 EndZ=0
    g1: LineSegment StartX=27 StartY=-2 StartZ=0 EndX=-43 EndY=-2 EndZ=0
    g2: LineSegment StartX=27 StartY=18 StartZ=0 EndX=27 EndY=-2 EndZ=0
    g3: LineSegment StartX=-43 StartY=18 StartZ=0 EndX=-43 EndY=-2 EndZ=0
    g4: LineSegment StartX=-8 StartY=20.77 StartZ=0 EndX=-8 EndY=17.2529 EndZ=0
  constraints (13):
    c: Horizontal(g1)
    c: DistanceY(g1) = -2
    c: DistanceY(g0) = 18
    c: Coincident(g2,g0)
    c: Vertical(g2)
    c: Coincident(g3,g0)
    c: Vertical(g3)
    c: Coincident(g3,g1)
    c: Coincident(g1,g2)
    c: Horizontal(g0)
    c: Symmetric(g0,g0,g4)
    c: DistanceX(g4) = -8
    c: Distance(g0) = 70
FEATURE [PartDesign::Pad] Pad005
  Direction = (1,1,1)
  Length = 12.7
  Length2 = 100
  Profile = -> Sketch029
  Type = 0
FEATURE [Sketcher::SketchObject] Sketch012  label="towerProper"
  FullyConstrained = false
  MapMode = 5
  Placement = pos=(0,0,12.7) rot=(0,0,1;0rad)
  Support = -> [Pad005]
  sketch-geometry (5):
    g0: LineSegment StartX=-26 StartY=18 StartZ=0 EndX=10 EndY=18 EndZ=0
    g1: LineSegment StartX=10 StartY=18 StartZ=0 EndX=10 EndY=1 EndZ=0
    g2: LineSegment StartX=10 StartY=1 StartZ=0 EndX=-26 EndY=1 EndZ=0
    g3: LineSegment StartX=-26 StartY=1 StartZ=0 EndX=-26 EndY=18 EndZ=0
    g4: LineSegment StartX=-8 StartY=21.6614 StartZ=0 EndX=-8 EndY=16.5307 EndZ=0
  constraints (13):
    c: Coincident(g0,g1)
    c: Coincident(g1,g2)
    c: Coincident(g2,g3)
    c: Coincident(g3,g0)
    c: Horizontal(g2)
    c: Vertical(g1)
    c: Vertical(g3)
    c: Distance(g0) = 36
    c: Vertical(g4)
    c: Symmetric(g0,g0,g4)
    c: DistanceX(g4) = -8
    c: DistanceY(g0) = 18
    c: DistanceY(g1) = 1
FEATURE [PartDesign::Pad] Pad006
  BaseFeature = -> Pad005
  Direction = (1,1,1)
  Length = 40
  Length2 = 100
  Profile = -> Sketch012
  Type = 0
FEATURE [PartDesign::Pocket] Pocket016
  BaseFeature = -> Pad006
  Length = 40
  Length2 = 100
  Profile = -> Sketch028
  Type = 0
FEATURE [PartDesign::Pocket] Pocket014
  BaseFeature = -> Pocket016
  Length = 5
  Length2 = 100
  Profile = -> Sketch025
  Type = 1
FEATURE [PartDesign::Pad] Pad007
  BaseFeature = -> Pocket014
  Direction = (1,1,1)
  Length = 6
  Length2 = 100
  Profile = -> Sketch027
  Type = 0
FEATURE [PartDesign::Pocket] Pocket017
  BaseFeature = -> Pad007
  Length = 2
  Length2 = 100
  Profile = -> Sketch026
  Reversed = true
  Type = 0
FEATURE [Sketcher::SketchObject] Sketch030  label="leadscrew"
  FullyConstrained = true
  MapMode = 5
  Placement = pos=(0,0,12.7) rot=(0,0,1;0rad)
  sketch-geometry (4):
    g0: ArcOfCircle CenterX=-8 CenterY=6 CenterZ=0 NormalX=0 NormalY=0 NormalZ=1 AngleXU=0 Radius=4.5 StartAngle=1e-16 EndAngle=3.14159
    g1: ArcOfCircle CenterX=-8 CenterY=4 CenterZ=0 NormalX=0 NormalY=0 NormalZ=1 AngleXU=0 Radius=4.5 StartAngle=3.14159 EndAngle=6.28319
    g2: LineSegment StartX=-12.5 StartY=6 StartZ=0 EndX=-12.5 EndY=4 EndZ=0
    g3: LineSegment StartX=-3.5 StartY=6 StartZ=0 EndX=-3.5 EndY=4 EndZ=0
  constraints (10):
    c: Tangent(g0,g3) = 1.5708
    c: Tangent(g0,g2) = -1.5708
    c: Tangent(g2,g1) = -1.5708
    c: Tangent(g3,g1) = 1.5708
    c: Vertical(g2)
    c: Equal(g0,g1)
    c: DistanceY(g1) = 4
    c: DistanceY(g0) = 6
    c: DistanceX(g0) = -8
    c: Diameter(g0) = 9
FEATURE [PartDesign::Pocket] Pocket015
  BaseFeature = -> Pocket017
  Length = 22
  Length2 = 100
  Profile = -> Sketch030
  Type = 4
FEATURE [Sketcher::SketchObject] Sketch013  label="counterbore"
  FullyConstrained = true
  MapMode = 5
  Placement = pos=(0,0,56.7) rot=(0,0,1;0rad)
  Support = -> [Pocket015]
  sketch-geometry (1):
    g0: Circle CenterX=-8 CenterY=5 CenterZ=0 NormalX=0 NormalY=0 NormalZ=1 AngleXU=0 Radius=9
  constraints (3):
    c: DistanceX(g0) = -8
    c: DistanceY(g0) = 5
    c: Diameter(g0) = 18
FEATURE [PartDesign::Pocket] Pocket018
  BaseFeature = -> Pocket015
  Length = 40
  Length2 = 100
  Profile = -> Sketch013
  Type = 0
FEATURE [PartDesign::Fillet] Fillet
  Base = -> Pocket018 [Edge83,Edge72]
  BaseFeature = -> Pocket018
  Radius = 1
  SupportTransform = false
FEATURE [PartDesign::Chamfer] Chamfer014
  Angle = 45
  Base = -> Fillet [Edge52,Edge57]
  BaseFeature = -> Fillet
  ChamferType = 0
  FlipDirection = false
  Size = 2
  Size2 = 1
  SupportTransform = false
FEATURE [PartDesign::Chamfer] Chamfer013
  Angle = 45
  Base = -> Chamfer014 [Edge135,Edge133]
  BaseFeature = -> Chamfer014
  ChamferType = 0
  FlipDirection = false
  Size = 4
  Size2 = 1
  SupportTransform = false
FEATURE [PartDesign::Body] Body002  label="Ztower"
  Group = -> [Sketch029,Pad005,Sketch028,Sketch030,Sketch027,Sketch026,Sketch025,Sketch012,Pad006,Pocket016,Pocket014,Pad007,Pocket017,Pocket015,Sketch013,Pocket018,Fillet,Chamfer014,Chamfer013]
  Origin = -> Origin002
  Placement = pos=(-0.401038,-43.0056,-24.8059) rot=(0.007695,0.882707,-0.469861;3.13341rad)
  Tip = -> Chamfer013
FEATURE [Sketcher::SketchObject] Sketch039
  FullyConstrained = true
  MapMode = 5
  Placement = pos=(0,0,0) rot=(0.57735,0.57735,0.57735;2.0944rad)
  Support = -> [YZ_Plane003]
  sketch-geometry (6):
    g0: LineSegment StartX=0 StartY=70 StartZ=0 EndX=23 EndY=70 EndZ=0
    g1: LineSegment StartX=23 StartY=70 StartZ=0 EndX=23 EndY=0 EndZ=0
    g2: LineSegment StartX=23 StartY=0 StartZ=0 EndX=5 EndY=0 EndZ=0
    g3: LineSegment StartX=5 StartY=0 StartZ=0 EndX=5 EndY=52.3 EndZ=0
    g4: LineSegment StartX=5 StartY=52.3 StartZ=0 EndX=0 EndY=57.3 EndZ=0
    g5: LineSegment StartX=0 StartY=57.3 StartZ=0 EndX=0 EndY=70 EndZ=0
  constraints (18):
    c: PointOnObject(g0,g-2)
    c: Horizontal(g0)
    c: Coincident(g0,g1)
    c: PointOnObject(g1,g-1)
    c: Vertical(g1)
    c: Coincident(g1,g2)
    c: Coincident(g3,g4)
    c: PointOnObject(g4,g-2)
    c: Coincident(g4,g5)
    c: Coincident(g5,g0)
    c: Coincident(g2,g3)
    c: Vertical(g3)
    c: Angle(g4) = 2.35619
    c: DistanceY(g0) = 70
    c: DistanceX(g3) = 5
    c: Distance(g2) = 18
    c: Horizontal(g2)
    c: Distance(g5) = 12.7
FEATURE [PartDesign::Pad] Pad008
  Direction = (1,1,1)
  Length = 80
  Length2 = 100
  Midplane = true
  Placement = pos=(0,0,0) rot=(0.57735,0.57735,0.57735;2.0944rad)
  Profile = -> Sketch039
  Type = 0
FEATURE [Sketcher::SketchObject] Sketch035  label="CouplerSlot"
  FullyConstrained = false
  MapMode = 5
  Placement = pos=(0,0,0) rot=(0.707107,0.707107,0;3.14159rad)
  Support = -> [Pad008]
  sketch-geometry (4):
    g0: ArcOfCircle CenterX=-8.8186 CenterY=8 CenterZ=0 NormalX=0 NormalY=0 NormalZ=1 AngleXU=0 Radius=8.5 StartAngle=1.5708 EndAngle=4.71239
    g1: ArcOfCircle CenterX=9 CenterY=8 CenterZ=0 NormalX=0 NormalY=0 NormalZ=1 AngleXU=0 Radius=8.5 StartAngle=4.71239 EndAngle=7.85398
    g2: LineSegment StartX=-8.8186 StartY=-0.5 StartZ=0 EndX=9 EndY=-0.5 EndZ=0
    g3: LineSegment StartX=-8.8186 StartY=16.5 StartZ=0 EndX=9 EndY=16.5 EndZ=0
  constraints (9):
    c: Tangent(g0,g3) = 1.5708
    c: Tangent(g0,g2) = -1.5708
    c: Tangent(g2,g1) = -1.5708
    c: Tangent(g3,g1) = 1.5708
    c: Horizontal(g2)
    c: Equal(g0,g1)
    c: DistanceY(g1) = 8
    c: DistanceX(g1) = 9
    c: Diameter(g1) = 17
FEATURE [PartDesign::Pocket] Pocket019
  BaseFeature = -> Pad008
  Length = 38
  Length2 = 100
  Placement = pos=(0,0,0) rot=(0.57735,0.57735,0.57735;2.0944rad)
  Profile = -> Sketch035
  Type = 0
FEATURE [Sketcher::SketchObject] Sketch042  label="BottomBoltHoles"
  FullyConstrained = true
  MapMode = 5
  Placement = pos=(-5.05e-14,4.66e-14,70) rot=(0,0,-1;1.5708rad)
  Support = -> [Pocket019]
  sketch-geometry (2):
    g0: Circle CenterX=-5 CenterY=30 CenterZ=0 NormalX=0 NormalY=0 NormalZ=1 AngleXU=0 Radius=2.35
    g1: Circle CenterX=-5 CenterY=-30 CenterZ=0 NormalX=0 NormalY=0 NormalZ=1 AngleXU=0 Radius=2.35
  constraints (5):
    c: Diameter(g1) = 4.7
    c: Equal(g1,g0)
    c: Symmetric(g1,g0,g-1)
    c: Distance(g0,g1) = 60
    c: DistanceX(g0) = -5
FEATURE [PartDesign::Pocket] Pocket020
  BaseFeature = -> Pocket019
  Length = 10
  Length2 = 100
  Placement = pos=(0,0,0) rot=(0.57735,0.57735,0.57735;2.0944rad)
  Profile = -> Sketch042
  Type = 0
FEATURE [Sketcher::SketchObject] Sketch044  label="TopBoltholes"
  FullyConstrained = true
  MapMode = 5
  Placement = pos=(2.2e-15,5,-5e-15) rot=(0.57735,0.57735,-0.57735;2.0944rad)
  Support = -> [Pocket020]
  sketch-geometry (2):
    g0: Circle CenterX=13 CenterY=30 CenterZ=0 NormalX=0 NormalY=0 NormalZ=1 AngleXU=0 Radius=1.4
    g1: Circle CenterX=13 CenterY=-30 CenterZ=0 NormalX=0 NormalY=0 NormalZ=1 AngleXU=0 Radius=1.4
  constraints (5):
    c: Symmetric(g1,g0,g-1)
    c: DistanceX(g0) = 13
    c: Diameter(g1) = 2.8
    c: Equal(g1,g0)
    c: Distance(g1,g0) = 60
FEATURE [Sketcher::SketchObject] Sketch045
  FullyConstrained = true
  MapMode = 5
  Support = -> [XY_Plane004]
  sketch-geometry (4):
    g0: LineSegment StartX=-40 StartY=32 StartZ=0 EndX=40 EndY=32 EndZ=0
    g1: LineSegment StartX=40 StartY=32 StartZ=0 EndX=40 EndY=-10 EndZ=0
    g2: LineSegment StartX=40 StartY=-10 StartZ=0 EndX=-40 EndY=-10 EndZ=0
    g3: LineSegment StartX=-40 StartY=-10 StartZ=0 EndX=-40 EndY=32 EndZ=0
  constraints (11):
    c: Coincident(g0,g1)
    c: Coincident(g1,g2)
    c: Coincident(g2,g3)
    c: Coincident(g3,g0)
    c: Horizontal(g2)
    c: Vertical(g1)
    c: Vertical(g3)
    c: Distance(g0) = 80
    c: Symmetric(g0,g0,g-2)
    c: Distance(g1) = 42
    c: DistanceY(g1) = -10
FEATURE [PartDesign::Pad] Pad009
  Direction = (1,1,1)
  Length = 5
  Length2 = 100
  Profile = -> Sketch045
  Type = 0
FEATURE [Sketcher::SketchObject] Sketch047
  FullyConstrained = true
  MapMode = 5
  Placement = pos=(0,0,0) rot=(1,0,0;3.14159rad)
  Support = -> [Pad009]
  sketch-geometry (17):
    g0: Circle CenterX=8 CenterY=-9 CenterZ=0 NormalX=0 NormalY=0 NormalZ=1 AngleXU=0 Radius=12
    g1: ArcOfCircle CenterX=-30 CenterY=-11 CenterZ=0 NormalX=0 NormalY=0 NormalZ=1 AngleXU=0 Radius=1.75 StartAngle=0 EndAngle=3.14159
    g2: ArcOfCircle CenterX=-30 CenterY=-15 CenterZ=0 NormalX=0 NormalY=0 NormalZ=1 AngleXU=0 Radius=1.75 StartAngle=3.14159 EndAngle=6.28319
    g3: LineSegment StartX=-31.75 StartY=-11 StartZ=0 EndX=-31.75 EndY=-15 EndZ=0
    g4: LineSegment StartX=-28.25 StartY=-11 StartZ=0 EndX=-28.25 EndY=-15 EndZ=0
    g5: ArcOfCircle CenterX=30 CenterY=-11 CenterZ=0 NormalX=0 NormalY=0 NormalZ=1 AngleXU=0 Radius=1.75 StartAngle=4e-16 EndAngle=3.14159
    g6: ArcOfCircle CenterX=30 CenterY=-15 CenterZ=0 NormalX=0 NormalY=0 NormalZ=1 AngleXU=0 Radius=1.75 StartAngle=3.14159 EndAngle=6.28319
    g7: LineSegment StartX=28.25 StartY=-11 StartZ=0 EndX=28.25 EndY=-15 EndZ=0
    g8: LineSegment StartX=31.75 StartY=-11 StartZ=0 EndX=31.75 EndY=-15 EndZ=0
    g9: Circle CenterX=-7.5 CenterY=6.5 CenterZ=0 NormalX=0 NormalY=0 NormalZ=1 AngleXU=0 Radius=1.75
    g10: Circle CenterX=23.5 CenterY=6.5 CenterZ=0 NormalX=0 NormalY=0 NormalZ=1 AngleXU=0 Radius=1.75
    g11: Circle CenterX=-7.5 CenterY=-24.5 CenterZ=0 NormalX=0 NormalY=0 NormalZ=1 AngleXU=0 Radius=1.75
    g12: Circle CenterX=23.5 CenterY=-24.5 CenterZ=0 NormalX=0 NormalY=0 NormalZ=1 AngleXU=0 Radius=1.75
    g13: LineSegment StartX=-7.5 StartY=6.5 StartZ=0 EndX=23.5 EndY=6.5 EndZ=0
    g14: LineSegment StartX=23.5 StartY=6.5 StartZ=0 EndX=23.5 EndY=-24.5 EndZ=0
    g15: LineSegment StartX=23.5 StartY=-24.5 StartZ=0 EndX=-7.5 EndY=-24.5 EndZ=0
    g16: LineSegment StartX=-7.5 StartY=-24.5 StartZ=0 EndX=-7.5 EndY=6.5 EndZ=0
  constraints (41):
    c: Diameter(g0) = 24
    c: DistanceX(g0) = 8
    c: DistanceY(g0) = -9
    c: Tangent(g1,g4) = 1.5708
    c: Tangent(g1,g3) = -1.5708
    c: Tangent(g3,g2) = -1.5708
    c: Tangent(g4,g2) = 1.5708
    c: Vertical(g3)
    c: Equal(g1,g2)
    c: Tangent(g5,g8) = 1.5708
    c: Tangent(g5,g7) = -1.5708
    c: Tangent(g7,g6) = -1.5708
    c: Tangent(g8,g6) = 1.5708
    c: Vertical(g7)
    c: Equal(g5,g6)
    c: Symmetric(g6,g2,g-2)
    c: Diameter(g2) = 3.5
    c: Equal(g2,g6)
    c: Distance(g8) = 4
    c: Distance(g4) = 4
    c: Distance(g5,g1) = 60
    c: Coincident(g13,g9)
    c: Coincident(g13,g10)
    c: Horizontal(g13)
    c: Coincident(g13,g14)
    c: Coincident(g14,g12)
    c: Vertical(g14)
    c: Coincident(g14,g15)
    c: Coincident(g15,g11)
    c: Horizontal(g15)
    c: Coincident(g15,g16)
    c: Coincident(g16,g13)
    c: Symmetric(g11,g10,g0)
    c: Equal(g15,g13)
    c: Distance(g15) = 31
    c: Equal(g15,g16)
    c: Diameter(g12) = 3.5
    c: Equal(g12,g10)
    c: Equal(g12,g9)
    c: Equal(g12,g11)
    c: DistanceY(g1) = -11
FEATURE [PartDesign::Pocket] Pocket022
  BaseFeature = -> Pad009
  Length = 5
  Length2 = 100
  Profile = -> Sketch047
  Type = 0
FEATURE [PartDesign::Pocket] Pocket023
  BaseFeature = -> Pocket020
  Length = 11
  Length2 = 100
  Placement = pos=(0,0,0) rot=(0.57735,0.57735,0.57735;2.0944rad)
  Profile = -> Sketch044
  Type = 0
FEATURE [Sketcher::SketchObject] Sketch048
  FullyConstrained = true
  MapMode = 5
  Placement = pos=(-2.74e-14,2.53e-14,38) rot=(0.707107,0.707107,0;3.14159rad)
  Support = -> [Pocket019]
  sketch-geometry (4):
    g0: ArcOfCircle CenterX=8 CenterY=8 CenterZ=0 NormalX=0 NormalY=0 NormalZ=1 AngleXU=0 Radius=5 StartAngle=1.5708 EndAngle=4.71239
    g1: ArcOfCircle CenterX=10 CenterY=8 CenterZ=0 NormalX=0 NormalY=0 NormalZ=1 AngleXU=0 Radius=5 StartAngle=4.71239 EndAngle=7.85398
    g2: LineSegment StartX=8 StartY=3 StartZ=0 EndX=10 EndY=3 EndZ=0
    g3: LineSegment StartX=8 StartY=13 StartZ=0 EndX=10 EndY=13 EndZ=0
  constraints (10):
    c: Tangent(g0,g3) = 1.5708
    c: Tangent(g0,g2) = -1.5708
    c: Tangent(g2,g1) = -1.5708
    c: Tangent(g3,g1) = 1.5708
    c: Horizontal(g2)
    c: Equal(g0,g1)
    c: Diameter(g1) = 10
    c: DistanceY(g1) = 8
    c: DistanceX(g1) = 10
    c: Distance(g0,g1) = 2
FEATURE [PartDesign::Pocket] Pocket024
  BaseFeature = -> Pocket023
  Length = 52
  Length2 = 100
  Placement = pos=(0,0,0) rot=(0.57735,0.57735,0.57735;2.0944rad)
  Profile = -> Sketch048
  Type = 0
FEATURE [PartDesign::Fillet] Fillet001
  Base = -> Pocket024 [Edge33,Edge35]
  BaseFeature = -> Pocket024
  Placement = pos=(0,0,0) rot=(0.57735,0.57735,0.57735;2.0944rad)
  Radius = 1
  SupportTransform = false
FEATURE [PartDesign::Body] Body003  label="BottomBlock"
  Group = -> [Sketch035,Sketch039,Pad008,Pocket019,Sketch042,Pocket020,Sketch044,Pocket023,Sketch048,Pocket024,Fillet001]
  Origin = -> Origin003
  Tip = -> Fillet001
FEATURE [Sketcher::SketchObject] Sketch049
  FullyConstrained = false
  MapMode = 5
  Placement = pos=(0,0,5) rot=(0,0,1;0rad)
  Support = -> [Pocket022]
  sketch-geometry (2):
    g0: Circle CenterX=-7.50929 CenterY=24.5615 CenterZ=0 NormalX=0 NormalY=0 NormalZ=1 AngleXU=0 Radius=3.47487
    g1: Circle CenterX=23.4765 CenterY=24.474 CenterZ=0 NormalX=0 NormalY=0 NormalZ=1 AngleXU=0 Radius=3.27743
FEATURE [PartDesign::Pocket] Pocket025
  BaseFeature = -> Pocket022
  Length = 2
  Length2 = 100
  Profile = -> Sketch049
  Type = 0
FEATURE [PartDesign::Body] Body004  label="StepperMount"
  Group = -> [Sketch045,Pad009,Sketch047,Pocket022,Sketch049,Pocket025]
  Origin = -> Origin004
  Placement = pos=(0,0,-5) rot=(0,0,1;0rad)
  Tip = -> Pocket025
FEATURE [Mesh::Feature] Mesh  label="Pocket025 (Meshed)"
FEATURE [Mesh::Feature] Mesh001  label="Fillet001 (Meshed)"
